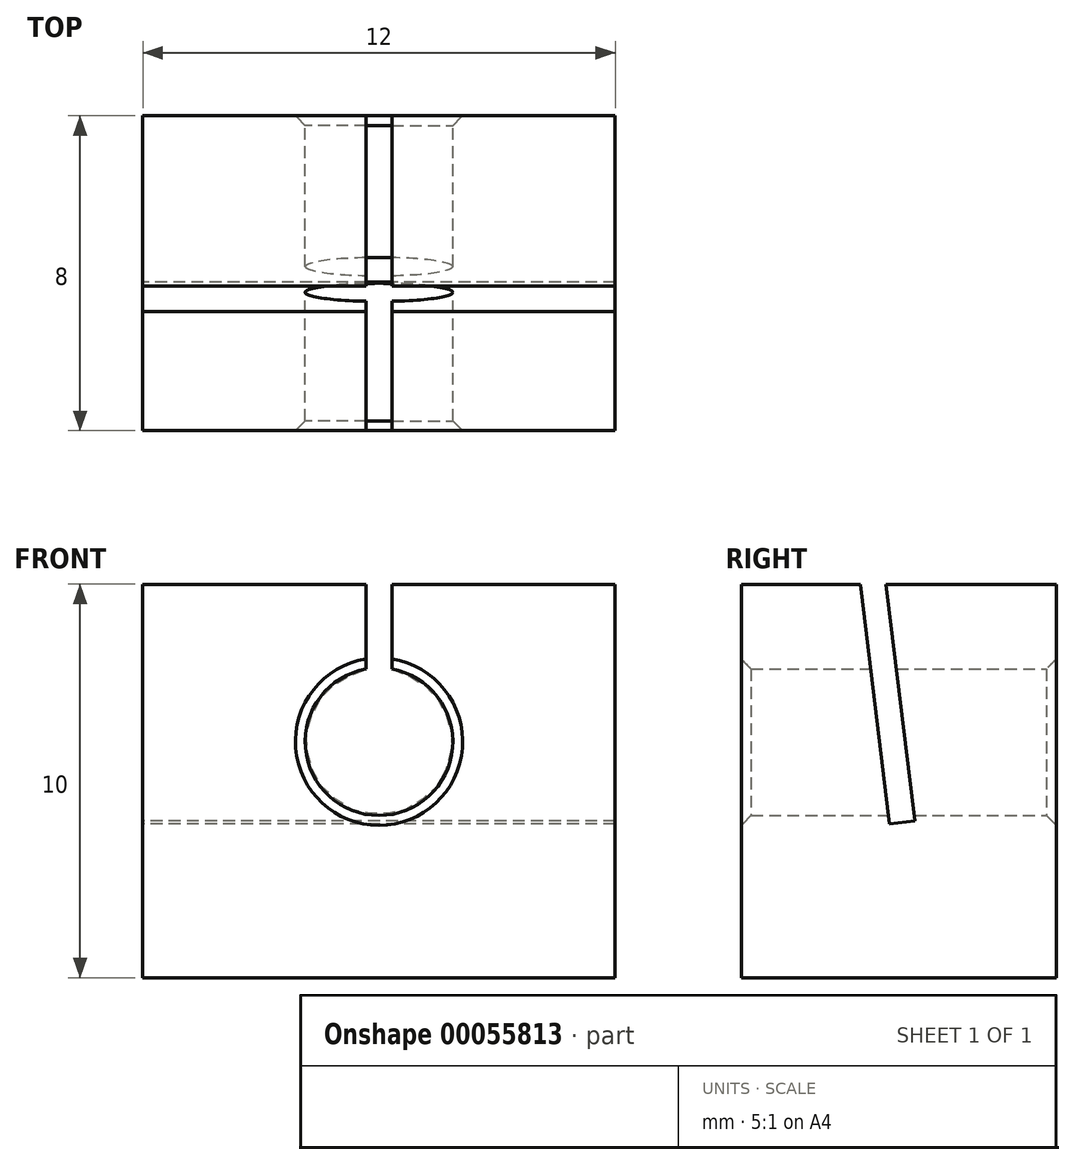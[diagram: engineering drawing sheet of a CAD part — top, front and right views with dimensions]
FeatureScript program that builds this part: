
annotation { "Feature Type Name" : "Feature", "Feature Type Description" : "" }
export const myFeature = defineFeature(function(context is Context, id is Id, definition is map)
    precondition{}
    {
        {
            var Q0;
            Q0=qCreatedBy(makeId("Front.planeOp"),FACE);
            var sketch = newSketch(context, id + "F0", { "sketchPlane" : qUnion([Q0])});
            skLineSegment(sketch, "E0.bottom", {"start": v(-30.1, 17.75) * mm, "end": v(-18.1, 17.75) * mm});
            skLineSegment(sketch, "E0.top", {"start": v(-30.1, 7.75) * mm, "end": v(-18.1, 7.75) * mm});
            skLineSegment(sketch, "E0.left", {"start": v(-30.1, 17.75) * mm, "end": v(-30.1, 7.75) * mm});
            skLineSegment(sketch, "E0.right", {"start": v(-18.1, 17.75) * mm, "end": v(-18.1, 7.75) * mm});
            skCircle(sketch, "E1", {"center": v(-24.1, 13.75) * mm, "radius": 1.88 * mm});
            skLineSegment(sketch, "E2.bottom", {"start": v(-24.43, 17.75) * mm, "end": v(-23.78, 17.75) * mm});
            skLineSegment(sketch, "E2.top", {"start": v(-24.43, 14.3) * mm, "end": v(-23.78, 14.3) * mm});
            skLineSegment(sketch, "E2.left", {"start": v(-24.43, 17.75) * mm, "end": v(-24.43, 14.3) * mm});
            skLineSegment(sketch, "E2.right", {"start": v(-23.78, 17.75) * mm, "end": v(-23.78, 14.3) * mm});
            skSolve(sketch);
        }
        {
            var Q0;
            Q0=makeQuery(id+"F0.imprint","IMPRINT",FACE,{"disambiguationData":[TD([[makeQuery(id+"F0.imprint","IMPRINT",EDGE,{"derivedFrom":sQuery(id+"F0.wireOp",EDGE,"E0.top")}),1.0]])]});
            extrude(context, id + "F1", {"entities" : qUnion([Q0]), "depth" : 8 * mm});
        }
        {
            var Q0;
            Q0=makeQuery(id+"F1.opExtrude","CAP_EDGE",EDGE,{"disambiguationData":[OSD([sQuery(id+"F0.wireOp",EDGE,"E1")])],"isStart":true});
            var Q1;
            Q1=makeQuery(id+"F1.opExtrude","CAP_EDGE",EDGE,{"disambiguationData":[OSD([sQuery(id+"F0.wireOp",EDGE,"E1")])],"isStart":false});
            var Q2;
            Q2=makeQuery(id+"F4gI3lwhnSt3bBE_1.boolean.opBoolean","INTERSECT",EDGE,{"derivedFrom":[makeQuery(id+"F1.opExtrude","SWEPT_FACE",FACE,{"disambiguationData":[OSD([sQuery(id+"F0.wireOp",EDGE,"E1")])]}),makeQuery(id+"F4gI3lwhnSt3bBE_1.opExtrude","SWEPT_FACE",FACE,{"disambiguationData":[OSD([sQuery(id+"FfPhiOSebWsNxAX_1.wireOp",EDGE,"1s1wXL8J-5XIA-0Qjp-JQ1D-nbg9SMgegVPp.bottom")])]})]});
            var Q3;
            Q3=makeQuery(id+"F4gI3lwhnSt3bBE_1.boolean.opBoolean","INTERSECT",EDGE,{"derivedFrom":[makeQuery(id+"F1.opExtrude","SWEPT_FACE",FACE,{"disambiguationData":[OSD([sQuery(id+"F0.wireOp",EDGE,"E1")])]}),makeQuery(id+"F4gI3lwhnSt3bBE_1.opExtrude","SWEPT_FACE",FACE,{"disambiguationData":[OSD([sQuery(id+"FfPhiOSebWsNxAX_1.wireOp",EDGE,"1s1wXL8J-5XIA-0Qjp-JQ1D-nbg9SMgegVPp.top")])]})]});
            var Q4;
            Q4=makeQuery(id+"F4gI3lwhnSt3bBE_1.boolean.opBoolean","COPY",EDGE,{"derivedFrom":makeQuery(id+"F4gI3lwhnSt3bBE_1.opExtrude","SWEPT_EDGE",EDGE,{"disambiguationData":[OSD([sQuery(id+"F0.wireOp",EDGE,"E0.bottom"),sQuery(id+"F0.wireOp",EDGE,"E0.right"),sQuery(id+"FfPhiOSebWsNxAX_1.wireOp",EDGE,"1s1wXL8J-5XIA-0Qjp-JQ1D-nbg9SMgegVPp.bottom"),sQuery(id+"FfPhiOSebWsNxAX_1.wireOp",EDGE,"1s1wXL8J-5XIA-0Qjp-JQ1D-nbg9SMgegVPp.right")])]})});
            var Q5;
            Q5=makeQuery(id+"F4gI3lwhnSt3bBE_1.boolean.opBoolean","COPY",EDGE,{"derivedFrom":makeQuery(id+"F4gI3lwhnSt3bBE_1.opExtrude","SWEPT_EDGE",EDGE,{"disambiguationData":[OSD([sQuery(id+"F0.wireOp",EDGE,"E0.bottom"),sQuery(id+"F0.wireOp",EDGE,"E0.right"),sQuery(id+"FfPhiOSebWsNxAX_1.wireOp",EDGE,"1s1wXL8J-5XIA-0Qjp-JQ1D-nbg9SMgegVPp.top"),sQuery(id+"FfPhiOSebWsNxAX_1.wireOp",EDGE,"1s1wXL8J-5XIA-0Qjp-JQ1D-nbg9SMgegVPp.right")])]})});
            var Q6;
            Q6=makeQuery(id+"F4gI3lwhnSt3bBE_1.boolean.opBoolean","COPY",EDGE,{"derivedFrom":makeQuery(id+"F4gI3lwhnSt3bBE_1.opExtrude","SWEPT_EDGE",EDGE,{"disambiguationData":[OSD([sQuery(id+"F0.wireOp",EDGE,"E0.bottom"),sQuery(id+"F0.wireOp",EDGE,"E0.left"),sQuery(id+"FfPhiOSebWsNxAX_1.wireOp",EDGE,"1s1wXL8J-5XIA-0Qjp-JQ1D-nbg9SMgegVPp.bottom"),sQuery(id+"FfPhiOSebWsNxAX_1.wireOp",EDGE,"1s1wXL8J-5XIA-0Qjp-JQ1D-nbg9SMgegVPp.left")])]})});
            var Q7;
            Q7=makeQuery(id+"F4gI3lwhnSt3bBE_1.boolean.opBoolean","COPY",EDGE,{"derivedFrom":makeQuery(id+"F4gI3lwhnSt3bBE_1.opExtrude","SWEPT_EDGE",EDGE,{"disambiguationData":[OSD([sQuery(id+"F0.wireOp",EDGE,"E0.bottom"),sQuery(id+"F0.wireOp",EDGE,"E0.left"),sQuery(id+"FfPhiOSebWsNxAX_1.wireOp",EDGE,"1s1wXL8J-5XIA-0Qjp-JQ1D-nbg9SMgegVPp.top"),sQuery(id+"FfPhiOSebWsNxAX_1.wireOp",EDGE,"1s1wXL8J-5XIA-0Qjp-JQ1D-nbg9SMgegVPp.left")])]})});
            var Q8;
            Q8=makeQuery(id+"F4gI3lwhnSt3bBE_1.boolean.opBoolean","COPY",EDGE,{"disambiguationData":[OD(0.0)],"derivedFrom":makeQuery(id+"F4gI3lwhnSt3bBE_1.opExtrude","CAP_EDGE",EDGE,{"disambiguationData":[OSD([sQuery(id+"FfPhiOSebWsNxAX_1.wireOp",EDGE,"1s1wXL8J-5XIA-0Qjp-JQ1D-nbg9SMgegVPp.top")])],"isStart":true})});
            var Q9;
            Q9=makeQuery(id+"F4gI3lwhnSt3bBE_1.boolean.opBoolean","COPY",EDGE,{"disambiguationData":[OD(1.0)],"derivedFrom":makeQuery(id+"F4gI3lwhnSt3bBE_1.opExtrude","CAP_EDGE",EDGE,{"disambiguationData":[OSD([sQuery(id+"FfPhiOSebWsNxAX_1.wireOp",EDGE,"1s1wXL8J-5XIA-0Qjp-JQ1D-nbg9SMgegVPp.top")])],"isStart":true})});
            var Q10;
            Q10=makeQuery(id+"F4gI3lwhnSt3bBE_1.boolean.opBoolean","COPY",EDGE,{"disambiguationData":[OD(1.0)],"derivedFrom":makeQuery(id+"F4gI3lwhnSt3bBE_1.opExtrude","CAP_EDGE",EDGE,{"disambiguationData":[OSD([sQuery(id+"FfPhiOSebWsNxAX_1.wireOp",EDGE,"1s1wXL8J-5XIA-0Qjp-JQ1D-nbg9SMgegVPp.bottom")])],"isStart":true})});
            var Q11;
            Q11=makeQuery(id+"F4gI3lwhnSt3bBE_1.boolean.opBoolean","COPY",EDGE,{"disambiguationData":[OD(0.0)],"derivedFrom":makeQuery(id+"F4gI3lwhnSt3bBE_1.opExtrude","CAP_EDGE",EDGE,{"disambiguationData":[OSD([sQuery(id+"FfPhiOSebWsNxAX_1.wireOp",EDGE,"1s1wXL8J-5XIA-0Qjp-JQ1D-nbg9SMgegVPp.bottom")])],"isStart":true})});
            var Q12;
            Q12=makeQuery(id+"F4gI3lwhnSt3bBE_1.boolean.opBoolean","INTERSECT",EDGE,{"derivedFrom":[makeQuery(id+"F1.opExtrude","SWEPT_FACE",FACE,{"disambiguationData":[OSD([sQuery(id+"F0.wireOp",EDGE,"E2.left")])]}),makeQuery(id+"F4gI3lwhnSt3bBE_1.opExtrude","SWEPT_FACE",FACE,{"disambiguationData":[OSD([sQuery(id+"FfPhiOSebWsNxAX_1.wireOp",EDGE,"1s1wXL8J-5XIA-0Qjp-JQ1D-nbg9SMgegVPp.bottom")])]})]});
            var Q13;
            Q13=makeQuery(id+"F4gI3lwhnSt3bBE_1.boolean.opBoolean","INTERSECT",EDGE,{"derivedFrom":[makeQuery(id+"F1.opExtrude","SWEPT_FACE",FACE,{"disambiguationData":[OSD([sQuery(id+"F0.wireOp",EDGE,"E2.right")])]}),makeQuery(id+"F4gI3lwhnSt3bBE_1.opExtrude","SWEPT_FACE",FACE,{"disambiguationData":[OSD([sQuery(id+"FfPhiOSebWsNxAX_1.wireOp",EDGE,"1s1wXL8J-5XIA-0Qjp-JQ1D-nbg9SMgegVPp.bottom")])]})]});
            var Q14;
            Q14=makeQuery(id+"F4gI3lwhnSt3bBE_1.boolean.opBoolean","INTERSECT",EDGE,{"derivedFrom":[makeQuery(id+"F1.opExtrude","SWEPT_FACE",FACE,{"disambiguationData":[OSD([sQuery(id+"F0.wireOp",EDGE,"E2.left")])]}),makeQuery(id+"F4gI3lwhnSt3bBE_1.opExtrude","SWEPT_FACE",FACE,{"disambiguationData":[OSD([sQuery(id+"FfPhiOSebWsNxAX_1.wireOp",EDGE,"1s1wXL8J-5XIA-0Qjp-JQ1D-nbg9SMgegVPp.top")])]})]});
            var Q15;
            Q15=makeQuery(id+"F4gI3lwhnSt3bBE_1.boolean.opBoolean","INTERSECT",EDGE,{"derivedFrom":[makeQuery(id+"F1.opExtrude","SWEPT_FACE",FACE,{"disambiguationData":[OSD([sQuery(id+"F0.wireOp",EDGE,"E2.right")])]}),makeQuery(id+"F4gI3lwhnSt3bBE_1.opExtrude","SWEPT_FACE",FACE,{"disambiguationData":[OSD([sQuery(id+"FfPhiOSebWsNxAX_1.wireOp",EDGE,"1s1wXL8J-5XIA-0Qjp-JQ1D-nbg9SMgegVPp.top")])]})]});
            chamfer(context, id + "F2", {"entities" : qUnion([Q0, Q1, Q2, Q3, Q4, Q5, Q6, Q7, Q8, Q9, Q10, Q11, Q12, Q13, Q14, Q15]), "width" : .25 * mm, "tangentPropagation" : true});
        }
        {
            var Q0;
            {var subQ0=sQuery(id+"F0.wireOp",EDGE,"E0.bottom");Q0=makeQuery(id+"F1.opExtrude","SWEPT_FACE",FACE,{"disambiguationData":[OSD([subQ0]),TDD([makeQuery(id+"F0.imprint","IMPRINT",EDGE,{"disambiguationData":[TD([[makeQuery(id+"F0.imprint","INTERSECT",VERTEX,{"derivedFrom":[subQ0,sQuery(id+"F0.wireOp",EDGE,"E0.left")]}),-1.0]])],"derivedFrom":subQ0})])]});}
            var Q1;
            {var subQ0=sQuery(id+"F0.wireOp",EDGE,"E0.bottom");Q1=makeQuery(id+"F1.opExtrude","CAP_EDGE",EDGE,{"disambiguationData":[OSD([subQ0]),TDD([makeQuery(id+"F0.imprint","IMPRINT",EDGE,{"disambiguationData":[TD([[makeQuery(id+"F0.imprint","INTERSECT",VERTEX,{"derivedFrom":[subQ0,sQuery(id+"F0.wireOp",EDGE,"E0.left")]}),-1.0]])],"derivedFrom":subQ0})])],"isStart":false});}
            cPlane(context, id + "F3", {"entities" : qUnion([Q0, Q1]), "cplaneType" : CPlaneType.LINE_ANGLE, "offset" : 150 * mm, "angle" : 7 * degree, "width" : 150 * mm, "height" : 150 * mm});
        }
        {
            var Q0;
            Q0=qCreatedBy(id+"F3.planeOp",FACE);
            var sketch = newSketch(context, id + "F4", { "sketchPlane" : qUnion([Q0])});
            skLineSegment(sketch, "E3.bottom", {"start": v(-15.5, 2.13) * mm, "end": v(-33.35, 2.13) * mm});
            skLineSegment(sketch, "E3.top", {"start": v(-15.5, 2.78) * mm, "end": v(-33.35, 2.78) * mm});
            skLineSegment(sketch, "E3.left", {"start": v(-15.5, 2.13) * mm, "end": v(-15.5, 2.78) * mm});
            skLineSegment(sketch, "E3.right", {"start": v(-33.35, 2.13) * mm, "end": v(-33.35, 2.78) * mm});
            skSolve(sketch);
        }
        {
            var Q0;
            Q0 = qSketchRegion(id + "F4", true);
            extrude(context, id + "F5", {"entities" : qUnion([Q0]), "operationType" : NewBodyOperationType.REMOVE, "depth" : 6.5 * mm});
        }
    });
